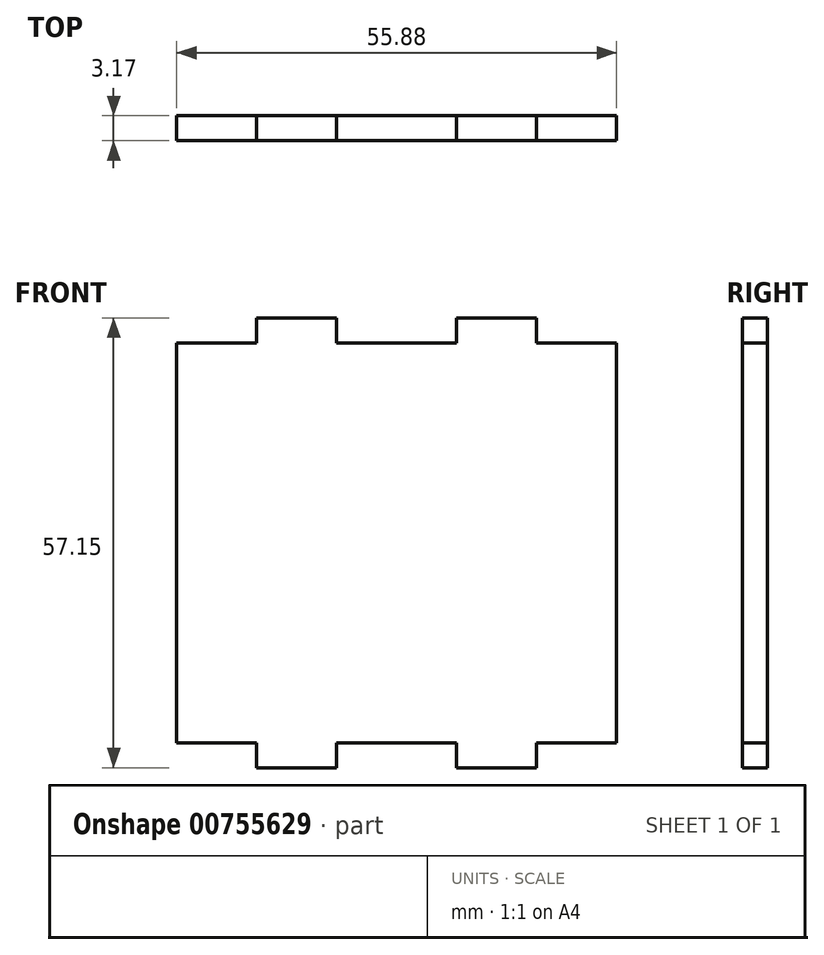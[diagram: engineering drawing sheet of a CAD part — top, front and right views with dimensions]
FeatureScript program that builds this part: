
annotation { "Feature Type Name" : "Feature", "Feature Type Description" : "" }
export const myFeature = defineFeature(function(context is Context, id is Id, definition is map)
    precondition{}
    {
        {
            var Q0;
            Q0=qCreatedBy(makeId("Front.planeOp"),FACE);
            var sketch = newSketch(context, id + "F0", { "sketchPlane" : qUnion([Q0])});
            skLineSegment(sketch, "E0.bottom", {"start": v(-60.87, 13.18) * mm, "end": v(-50.7, 13.18) * mm});
            skLineSegment(sketch, "E0.top", {"start": v(-60.87, -37.62) * mm, "end": v(-50.7, -37.62) * mm});
            skLineSegment(sketch, "E0.left", {"start": v(-60.87, 13.18) * mm, "end": v(-60.87, -37.62) * mm});
            skLineSegment(sketch, "E0.right", {"start": v(-4.99, 13.18) * mm, "end": v(-4.99, -37.62) * mm});
            skLineSegment(sketch, "E1.top", {"start": v(-50.7, -40.8) * mm, "end": v(-40.55, -40.8) * mm});
            skLineSegment(sketch, "E1.left", {"start": v(-50.7, -37.62) * mm, "end": v(-50.7, -40.8) * mm});
            skLineSegment(sketch, "E1.right", {"start": v(-40.55, -37.62) * mm, "end": v(-40.55, -40.8) * mm});
            skLineSegment(sketch, "E2.top", {"start": v(-25.3, -40.8) * mm, "end": v(-15.15, -40.8) * mm});
            skLineSegment(sketch, "E2.left", {"start": v(-25.3, -37.62) * mm, "end": v(-25.3, -40.8) * mm});
            skLineSegment(sketch, "E2.right", {"start": v(-15.15, -37.62) * mm, "end": v(-15.15, -40.8) * mm});
            skLineSegment(sketch, "E3.trimOffspring", {"start": v(-15.15, -37.62) * mm, "end": v(-4.99, -37.62) * mm});
            skLineSegment(sketch, "E4.trimOffspring", {"start": v(-40.55, -37.62) * mm, "end": v(-25.3, -37.62) * mm});
            skLineSegment(sketch, "E5.MirrorCS", {"start": v(-50.7, 16.36) * mm, "end": v(-40.55, 16.36) * mm});
            skLineSegment(sketch, "E6.MirrorCS", {"start": v(-25.3, 16.36) * mm, "end": v(-15.15, 16.36) * mm});
            skLineSegment(sketch, "E7", {"start": v(-50.7, 16.36) * mm, "end": v(-50.7, 13.18) * mm});
            skLineSegment(sketch, "E8", {"start": v(-40.55, 16.36) * mm, "end": v(-40.55, 13.18) * mm});
            skLineSegment(sketch, "E9", {"start": v(-25.3, 16.36) * mm, "end": v(-25.3, 13.18) * mm});
            skLineSegment(sketch, "E10", {"start": v(-15.15, 13.18) * mm, "end": v(-15.15, 16.36) * mm});
            skLineSegment(sketch, "E11.trimOffspring", {"start": v(-40.55, 13.18) * mm, "end": v(-25.3, 13.18) * mm});
            skLineSegment(sketch, "E12.trimOffspring", {"start": v(-15.15, 13.18) * mm, "end": v(-4.99, 13.18) * mm});
            skPoint(sketch, "E13.end.orphan", {"position": v(-4.99, -12.22) * mm});
            skPoint(sketch, "E13.start.orphan", {"position": v(-60.87, -12.22) * mm});
            skSolve(sketch);
        }
        {
            var Q0;
            Q0=makeQuery(id+"F0.imprint","IMPRINT",FACE,{"disambiguationData":[TD([[makeQuery(id+"F0.imprint","IMPRINT",EDGE,{"derivedFrom":sQuery(id+"F0.wireOp",EDGE,"E0.bottom")}),-1.0]])]});
            extrude(context, id + "F1", {"entities" : qUnion([Q0]), "depth" : 3.17 * mm, "offsetDistance" : 25.4 * mm});
        }
    });
